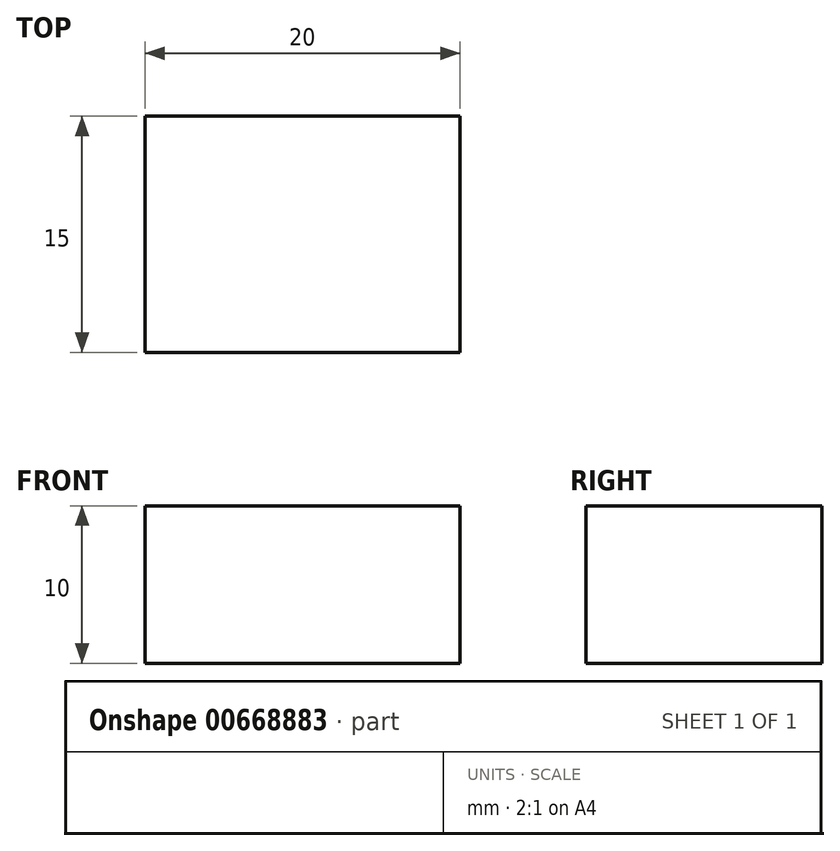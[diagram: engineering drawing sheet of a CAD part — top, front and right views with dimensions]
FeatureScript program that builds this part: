
annotation { "Feature Type Name" : "Feature", "Feature Type Description" : "" }
export const myFeature = defineFeature(function(context is Context, id is Id, definition is map)
    precondition{}
    {
        {
            var Q0;
            Q0=qCreatedBy(makeId("Front.planeOp"),FACE);
            var sketch = newSketch(context, id + "F0", { "sketchPlane" : qUnion([Q0])});
            skLineSegment(sketch, "E0.bottom", {"start": v(0, 0) * mm, "end": v(20, 0) * mm});
            skLineSegment(sketch, "E0.top", {"start": v(0, 10) * mm, "end": v(20, 10) * mm});
            skLineSegment(sketch, "E0.left", {"start": v(0, 0) * mm, "end": v(0, 10) * mm});
            skLineSegment(sketch, "E0.right", {"start": v(20, 0) * mm, "end": v(20, 10) * mm});
            skSolve(sketch);
        }
        {
            var Q0;
            Q0 = qSketchRegion(id + "F0", true);
            extrude(context, id + "F1", {"entities" : qUnion([Q0]), "endBound" : BoundingType.SYMMETRIC, "depth" : 15 * mm, "offsetDistance" : 25 * mm});
        }
    });
